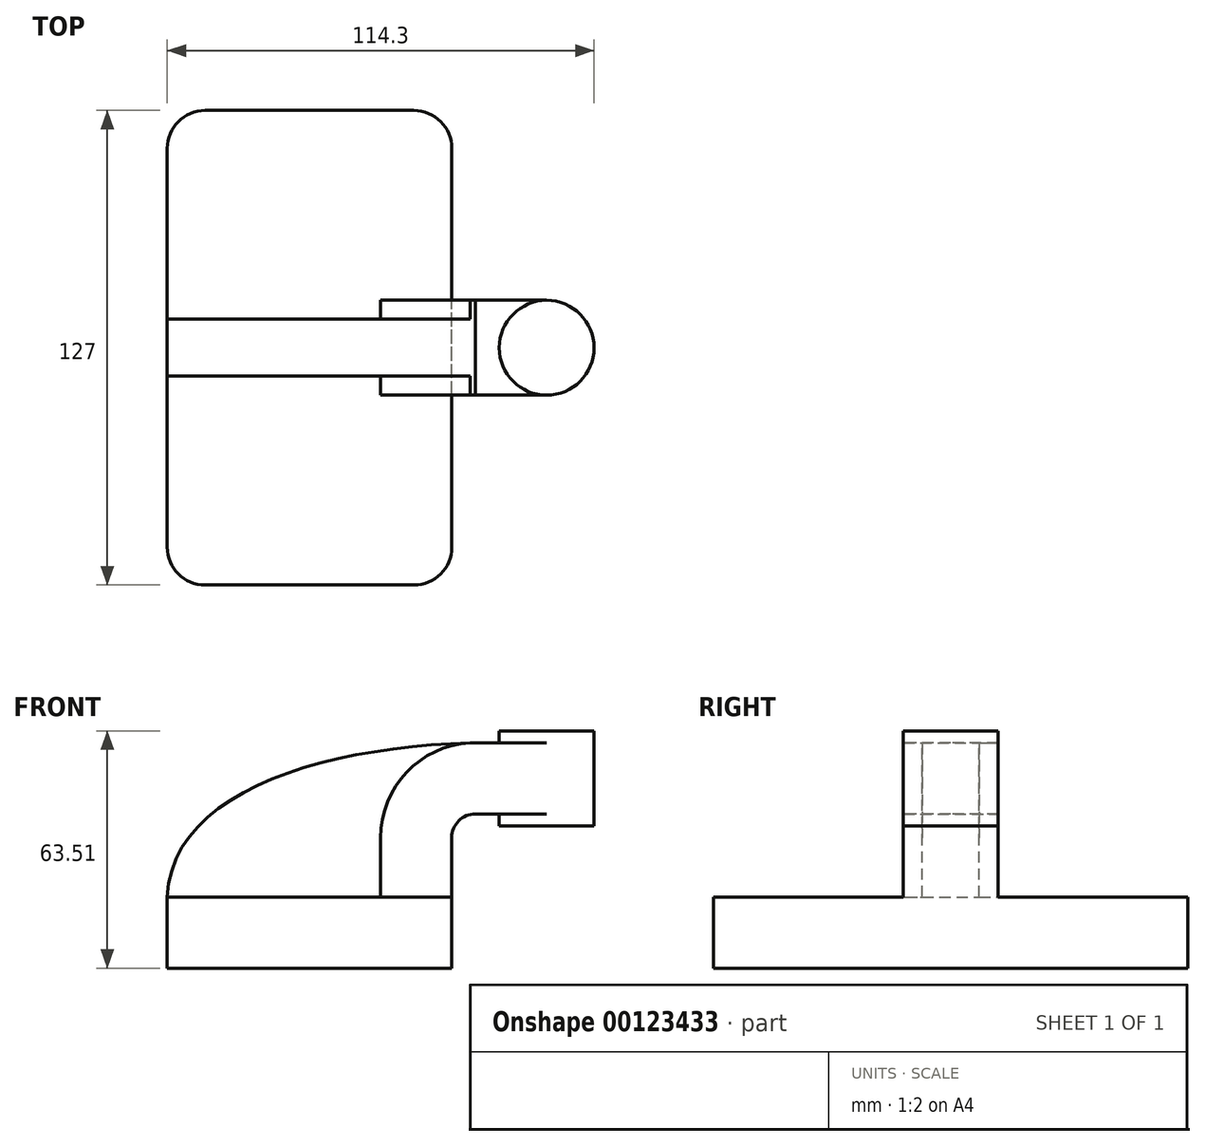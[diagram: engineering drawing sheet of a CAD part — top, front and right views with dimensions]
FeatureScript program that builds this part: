
annotation { "Feature Type Name" : "Feature", "Feature Type Description" : "" }
export const myFeature = defineFeature(function(context is Context, id is Id, definition is map)
    precondition{}
    {
        {
            var Q0;
            Q0=qCreatedBy(makeId("Front.planeOp"),FACE);
            var sketch = newSketch(context, id + "F0", { "sketchPlane" : qUnion([Q0])});
            skLineSegment(sketch, "E0.bottom", {"start": v(38.1, 9.53) * mm, "end": v(-38.1, 9.53) * mm});
            skLineSegment(sketch, "E0.top", {"start": v(38.1, -9.52) * mm, "end": v(-38.1, -9.52) * mm});
            skLineSegment(sketch, "E0.left", {"start": v(38.1, 9.53) * mm, "end": v(38.1, -9.52) * mm});
            skLineSegment(sketch, "E0.right", {"start": v(-38.1, 9.53) * mm, "end": v(-38.1, -9.52) * mm});
            skPoint(sketch, "E0.middle", {"position": v(0, 0) * mm});
            skLineSegment(sketch, "E1.bottom", {"start": v(76.2, 53.98) * mm, "end": v(50.8, 53.98) * mm});
            skLineSegment(sketch, "E1.top", {"start": v(76.2, 28.58) * mm, "end": v(50.8, 28.58) * mm});
            skLineSegment(sketch, "E1.left", {"start": v(76.2, 53.98) * mm, "end": v(76.2, 28.58) * mm});
            skLineSegment(sketch, "E1.right", {"start": v(50.8, 53.98) * mm, "end": v(50.8, 28.58) * mm});
            skPoint(sketch, "E1.middle", {"position": v(63.5, 41.28) * mm});
            skLineSegment(sketch, "E2", {"start": v(38.1, 9.53) * mm, "end": v(38.1, 25.4) * mm});
            skLineSegment(sketch, "E3", {"start": v(44.45, 31.75) * mm, "end": v(63.5, 31.75) * mm});
            skArc(sketch, "E4", {"start": v(38.1, 25.4) * mm, "mid": v(39.96, 29.9) * mm, "end": v(44.45, 31.75) * mm});
            skLineSegment(sketch, "E5.0", {"start": v(44.45, 50.8) * mm, "end": v(63.5, 50.8) * mm});
            skArc(sketch, "E5.1", {"start": v(19.05, 25.4) * mm, "mid": v(26.49, 43.36) * mm, "end": v(44.45, 50.8) * mm});
            skLineSegment(sketch, "E5.2", {"start": v(19.05, 9.53) * mm, "end": v(19.05, 25.4) * mm});
            skLineSegment(sketch, "E6", {"start": v(63.5, 28.58) * mm, "end": v(63.5, 53.98) * mm});
            skLineSegment(sketch, "E7", {"start": v(63.5, 41.28) * mm, "end": v(63.5, 41.28) * mm});
            skFitSpline(sketch, "E8", {"points": [v(-38.1, 9.52) * mm, v(44.45, 50.8) * mm], "startDerivative": vector(3.75, 85.37) * mm, "endDerivative": vector(121.13, 3.02) * mm});
            skSolve(sketch);
        }
        {
            var Q0;
            Q0=makeQuery(id+"F0.imprint","IMPRINT",FACE,{"disambiguationData":[TD([[makeQuery(id+"F0.imprint","IMPRINT",EDGE,{"derivedFrom":sQuery(id+"F0.wireOp",EDGE,"E0.top")}),-1.0]])]});
            extrude(context, id + "F1", {"entities" : qUnion([Q0]), "endBound" : BoundingType.SYMMETRIC, "depth" : 127 * mm});
        }
        {
            var Q0;
            {var subQ4=sQuery(id+"F0.wireOp",EDGE,"E2");Q0=makeQuery(id+"F0.imprint","IMPRINT",FACE,{"disambiguationData":[TD([[makeQuery(id+"F0.imprint","IMPRINT",EDGE,{"derivedFrom":subQ4}),1.0]])]});}
            var Q1;
            {var subQ0=sQuery(id+"F0.wireOp",EDGE,"E5.0");var subQ1=sQuery(id+"F0.wireOp",EDGE,"E1.right");var subQ2=makeQuery(id+"F0.imprint","INTERSECT",VERTEX,{"derivedFrom":[subQ1,subQ0]});Q1=makeQuery(id+"F0.imprint","IMPRINT",FACE,{"disambiguationData":[TD([[makeQuery(id+"F0.imprint","IMPRINT",EDGE,{"disambiguationData":[TD([[subQ2,-1.0]])],"derivedFrom":subQ1}),1.0]])]});}
            extrude(context, id + "F2", {"entities" : qUnion([Q0, Q1]), "operationType" : NewBodyOperationType.ADD, "endBound" : BoundingType.SYMMETRIC, "depth" : 25.4 * mm});
        }
        {
            var Q0;
            {var subQ3=sQuery(id+"F0.wireOp",EDGE,"E5.2");Q0=makeQuery(id+"F0.imprint","IMPRINT",FACE,{"disambiguationData":[TD([[makeQuery(id+"F0.imprint","IMPRINT",EDGE,{"derivedFrom":subQ3}),1.0]])]});}
            extrude(context, id + "F3", {"entities" : qUnion([Q0]), "operationType" : NewBodyOperationType.ADD, "endBound" : BoundingType.SYMMETRIC, "depth" : 15.24 * mm});
        }
        {
            var Q0;
            {var subQ0=sQuery(id+"F0.wireOp",EDGE,"E1.left");Q0=makeQuery(id+"F0.imprint","IMPRINT",FACE,{"disambiguationData":[TD([[makeQuery(id+"F0.imprint","IMPRINT",EDGE,{"derivedFrom":subQ0}),-1.0]])]});}
            var Q1;
            Q1=sQuery(id+"F0.wireOp",EDGE,"E6");
            revolve(context, id + "F4", {"operationType" : NewBodyOperationType.ADD, "entities" : qUnion([Q0]), "axis" : qUnion([Q1]), "revolveType" : RevolveType.FULL});
        }
        {
            var Q0;
            Q0=makeQuery(id+"F1.opExtrude","CAP_EDGE",EDGE,{"disambiguationData":[OSD([sQuery(id+"F0.wireOp",EDGE,"E0.left")])],"isStart":false});
            var Q1;
            Q1=makeQuery(id+"F1.opExtrude","CAP_EDGE",EDGE,{"disambiguationData":[OSD([sQuery(id+"F0.wireOp",EDGE,"E0.right")])],"isStart":false});
            var Q2;
            Q2=makeQuery(id+"F1.opExtrude","CAP_EDGE",EDGE,{"disambiguationData":[OSD([sQuery(id+"F0.wireOp",EDGE,"E0.right")])],"isStart":true});
            var Q3;
            Q3=makeQuery(id+"F1.opExtrude","CAP_EDGE",EDGE,{"disambiguationData":[OSD([sQuery(id+"F0.wireOp",EDGE,"E0.left")])],"isStart":true});
            fillet(context, id + "F5", {"entities" : qUnion([Q0, Q1, Q2, Q3]), "radius" : 10.16 * mm, "tangentPropagation" : true, "allowEdgeOverflow" : false});
        }
    });
